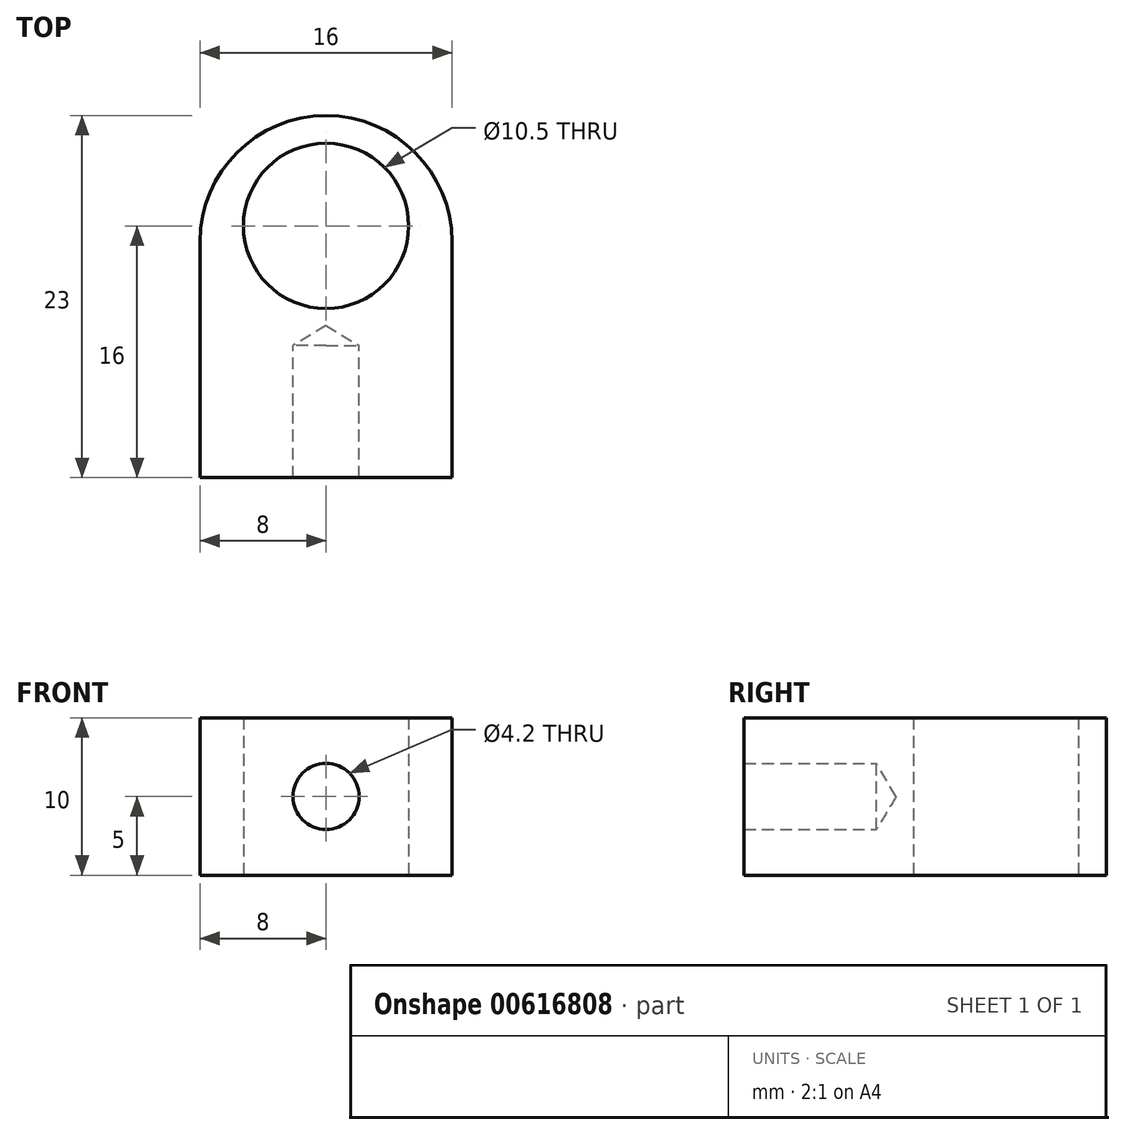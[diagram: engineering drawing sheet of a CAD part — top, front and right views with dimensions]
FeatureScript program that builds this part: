
annotation { "Feature Type Name" : "Feature", "Feature Type Description" : "" }
export const myFeature = defineFeature(function(context is Context, id is Id, definition is map)
    precondition{}
    {
        {
            var Q0;
            Q0=qCreatedBy(makeId("Top.planeOp"),FACE);
            var sketch = newSketch(context, id + "F0", { "sketchPlane" : qUnion([Q0])});
            skLineSegment(sketch, "E0.bottom", {"start": v(0, 11.5) * mm, "end": v(0, 11.5) * mm});
            skLineSegment(sketch, "E0.top", {"start": v(8, -11.5) * mm, "end": v(-8, -11.5) * mm});
            skLineSegment(sketch, "E0.left", {"start": v(8, 3.5) * mm, "end": v(8, -11.5) * mm});
            skLineSegment(sketch, "E0.right", {"start": v(-8, 3.5) * mm, "end": v(-8, -11.5) * mm});
            skPoint(sketch, "E0.middle", {"position": v(0, 0) * mm});
            skCircle(sketch, "E1", {"center": v(0, 4.5) * mm, "radius": 5.25 * mm});
            skPoint(sketch, "E2.visualSharp", {"position": v(-8, 11.5) * mm});
            skArc(sketch, "E2.filletArc", {"start": v(0, 11.5) * mm, "mid": v(-5.66, 9.16) * mm, "end": v(-8, 3.5) * mm});
            skPoint(sketch, "E3.visualSharp", {"position": v(8, 11.5) * mm});
            skArc(sketch, "E3.filletArc", {"start": v(8, 3.5) * mm, "mid": v(5.66, 9.16) * mm, "end": v(0, 11.5) * mm});
            skSolve(sketch);
        }
        {
            var Q0;
            Q0 = qSketchRegion(id + "F0", true);
            extrude(context, id + "F1", {"entities" : qUnion([Q0]), "depth" : 10 * mm, "offsetDistance" : 25 * mm});
        }
        {
            var Q0;
            Q0=makeQuery(id+"F1.opExtrude","SWEPT_FACE",FACE,{"disambiguationData":[OSD([sQuery(id+"F0.wireOp",EDGE,"E0.top")])]});
            var sketch = newSketch(context, id + "F2", { "sketchPlane" : qUnion([Q0])});
            skPoint(sketch, "E4", {"position": v(0, 5) * mm});
            skSolve(sketch);
        }
        {
            var Q0;
            Q0=sQuery(id+"F2.wireOp",VERTEX,"E4");
            var Q1;
            Q1=makeQuery(id+"F1.opExtrude","SWEPT_BODY",BODY,{"disambiguationData":[OSD([sQuery(id+"F0.wireOp",EDGE,"E0.top"),sQuery(id+"F0.wireOp",EDGE,"E0.left"),sQuery(id+"F0.wireOp",EDGE,"E0.right"),sQuery(id+"F0.wireOp",EDGE,"E1"),sQuery(id+"F0.wireOp",EDGE,"E2.filletArc"),sQuery(id+"F0.wireOp",EDGE,"E3.filletArc")])]});
            hole(context, id + "F3", {"style" : HoleStyle.SIMPLE, "endStyle" : HoleEndStyle.BLIND, "standardTappedOrClearance" : lookupTablePath({ "standard" : "ISO", "engagement" : "75%", "pitch" : "0.8 mm", "size" : "M5", "type" : "Tapped" }), "standardBlindInLast" : lookupTablePath({ "standard" : "ISO", "engagement" : "75%", "pitch" : "0.8 mm", "size" : "M5", "type" : "Tapped" }), "holeDiameter" : 4.2 * mm, "majorDiameter" : 5 * mm, "showTappedDepth" : true, "holeDepth" : 8.4 * mm, "tappedDepth" : 6 * mm, "tapClearance" : 3, "locations" : qUnion([Q0]), "scope" : qUnion([Q1]), "startStyle" : HoleStartStyle.PART});
        }
    });
